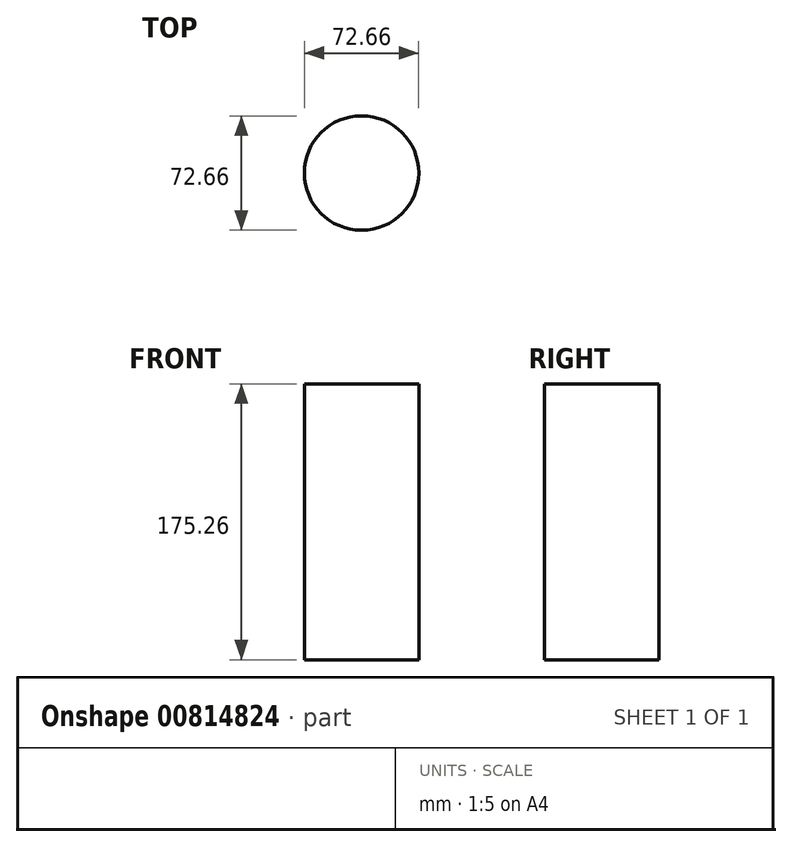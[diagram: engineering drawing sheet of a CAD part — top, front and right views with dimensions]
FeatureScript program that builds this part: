
annotation { "Feature Type Name" : "Feature", "Feature Type Description" : "" }
export const myFeature = defineFeature(function(context is Context, id is Id, definition is map)
    precondition{}
    {
        {
            var Q0;
            Q0=qCreatedBy(makeId("Top.planeOp"),FACE);
            var sketch = newSketch(context, id + "F0", { "sketchPlane" : qUnion([Q0])});
            skCircle(sketch, "E0", {"center": v(0, 0) * mm, "radius": 36.33 * mm});
            skSolve(sketch);
        }
        {
            var Q0;
            Q0=makeQuery(id+"F0.imprint","IMPRINT",FACE,{"disambiguationData":[TD([[makeQuery(id+"F0.imprint","IMPRINT",EDGE,{"derivedFrom":sQuery(id+"F0.wireOp",EDGE,"E0")}),1.0]])]});
            extrude(context, id + "F1", {"entities" : qUnion([Q0]), "depth" : 175.26 * mm, "offsetDistance" : 25.4 * mm});
        }
    });
